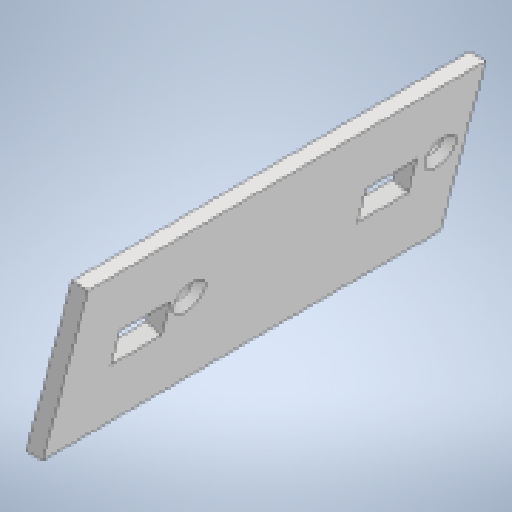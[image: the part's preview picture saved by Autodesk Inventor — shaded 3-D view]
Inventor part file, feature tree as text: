
AUTODESK INVENTOR PART (.ipt)
format: ipt  version: 2023 (Build 270158000, 158)  size: 176,640 bytes
history: native  units: in
note: dims shown in document units (in); Inventor stores cm internally (conversion verified against a paired STEP export)
features: reference x11, other x8, sketch x5, extrude x4, hole x1, projected_geometry x1
ambient origin geometry x8: Origin, YZ Plane, XZ Plane, XY Plane, X Axis, Y Axis, Z Axis, Center Point
bodies: Body1 (feature_tree)
feature tree (30):
  other  "Bryła1"
  extrude  "Wyciągnięcie proste1"  Depth=0.0787in
  extrude  "Wyciągnięcie proste2"  TaperAngle=75.0deg  [1 undecoded]
  extrude  "Wyciągnięcie proste3"  Depth=0.0787in
  extrude  "Wyciągnięcie proste4"  Depth=0.7874in
  hole  "Otwór1"  [1 undecoded]
  sketch  "Szkic1"
  reference  "Odniesienie1"
  sketch  "Szkic2"
  reference  "Odniesienie2"
  reference  "Odniesienie3"
  reference  "Odniesienie4"
  reference  "Odniesienie5"
  sketch  "Szkic3"
  projected_geometry  "Pętla rzutowana1"
  reference  "Odniesienie6"
  sketch  "Szkic4"
  reference  "Odniesienie7"
  reference  "Odniesienie8"
  sketch  "Szkic5"
  reference  "Odniesienie9"
  reference  "Odniesienie10"
  reference  "Odniesienie11"
  other  "<userpath>\Documents\PROJECTS - repos\Stratos---MicroSumo\mechanics\byk_alternator.iam"
  other  "byk_alternator.iam"
  other  "podstawa:1"
  other  "<userpath>\Documents\Inventor\MikroNalesnik\byk_alternator.iam"
  other  "TOF_VL53L0X (1):2"
  other  "TOF_VL53L0X (1):1"
  other  "dach:1"
note: 2 required parameter values undecoded (feature->parameter linkage not recoverable at this tier; creation-order binding heuristic only, values carry confidence <= 0.55)
